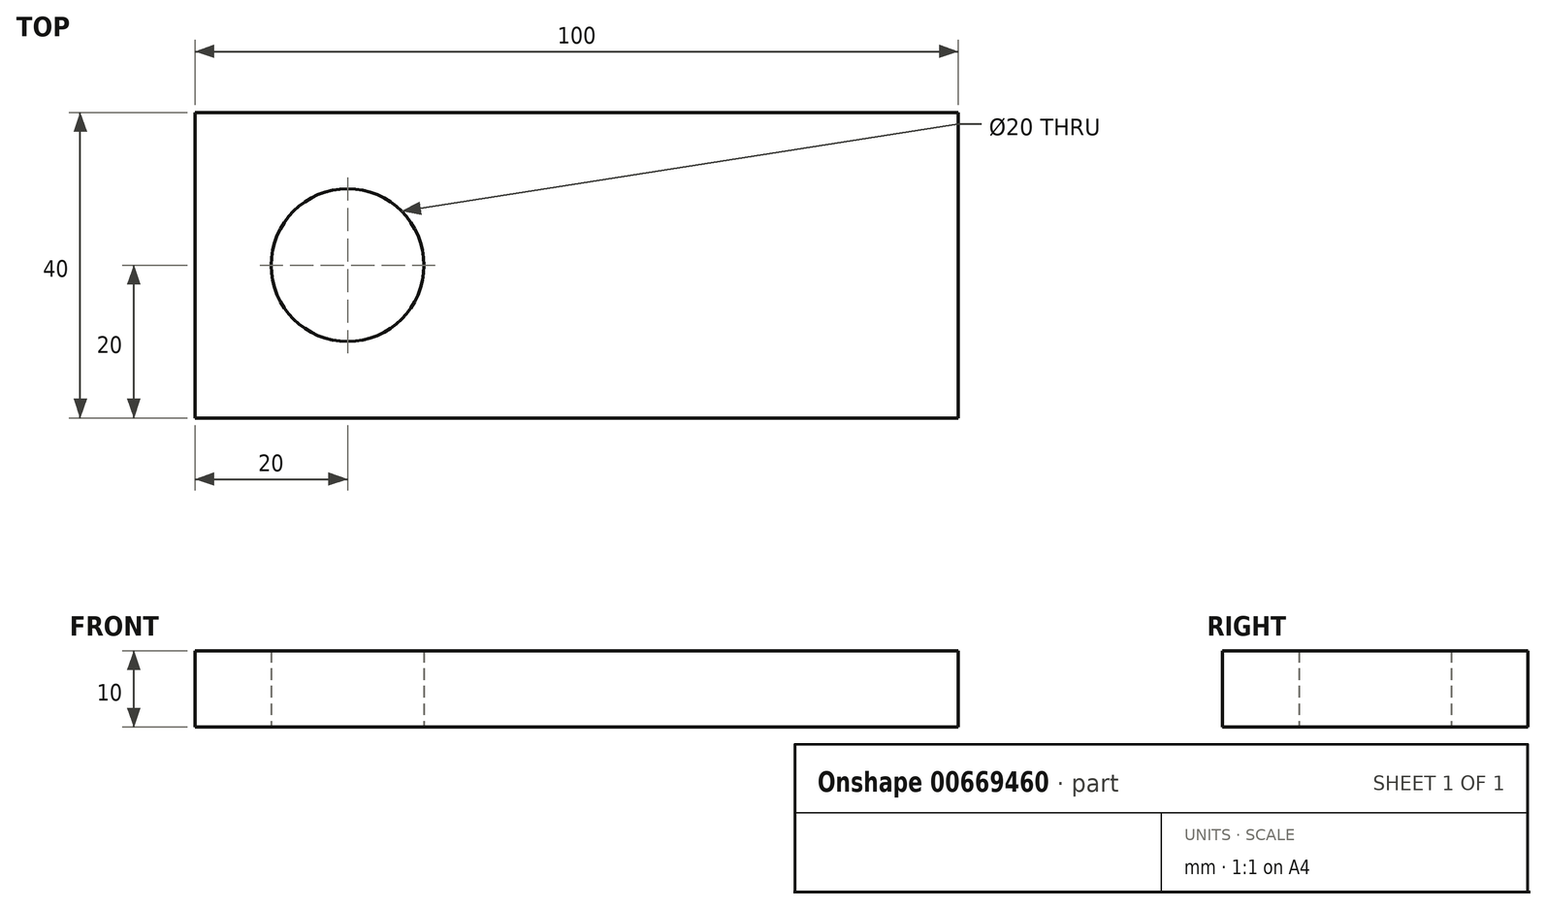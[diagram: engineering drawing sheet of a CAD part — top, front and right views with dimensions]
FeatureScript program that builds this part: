
annotation { "Feature Type Name" : "Feature", "Feature Type Description" : "" }
export const myFeature = defineFeature(function(context is Context, id is Id, definition is map)
    precondition{}
    {
        {
            var Q0;
            Q0=qCreatedBy(makeId("Top.planeOp"),FACE);
            var sketch = newSketch(context, id + "F0", { "sketchPlane" : qUnion([Q0])});
            skLineSegment(sketch, "E0", {"start": v(0, 0) * mm, "end": v(0, 40) * mm});
            skLineSegment(sketch, "E1", {"start": v(0, 40) * mm, "end": v(100, 40) * mm});
            skLineSegment(sketch, "E2", {"start": v(100, 40) * mm, "end": v(100, 0) * mm});
            skLineSegment(sketch, "E3", {"start": v(100, 0) * mm, "end": v(0, 0) * mm});
            skPoint(sketch, "E4", {"position": v(20, 20) * mm});
            skCircle(sketch, "E5", {"center": v(20, 20) * mm, "radius": 10 * mm});
            skSolve(sketch);
        }
        {
            var Q0;
            Q0=makeQuery(id+"F0.imprint","IMPRINT",FACE,{"disambiguationData":[TD([[makeQuery(id+"F0.imprint","IMPRINT",EDGE,{"derivedFrom":sQuery(id+"F0.wireOp",EDGE,"E0")}),-1.0]])]});
            extrude(context, id + "F1", {"entities" : qUnion([Q0]), "depth" : 10 * mm, "offsetDistance" : 25 * mm});
        }
    });
